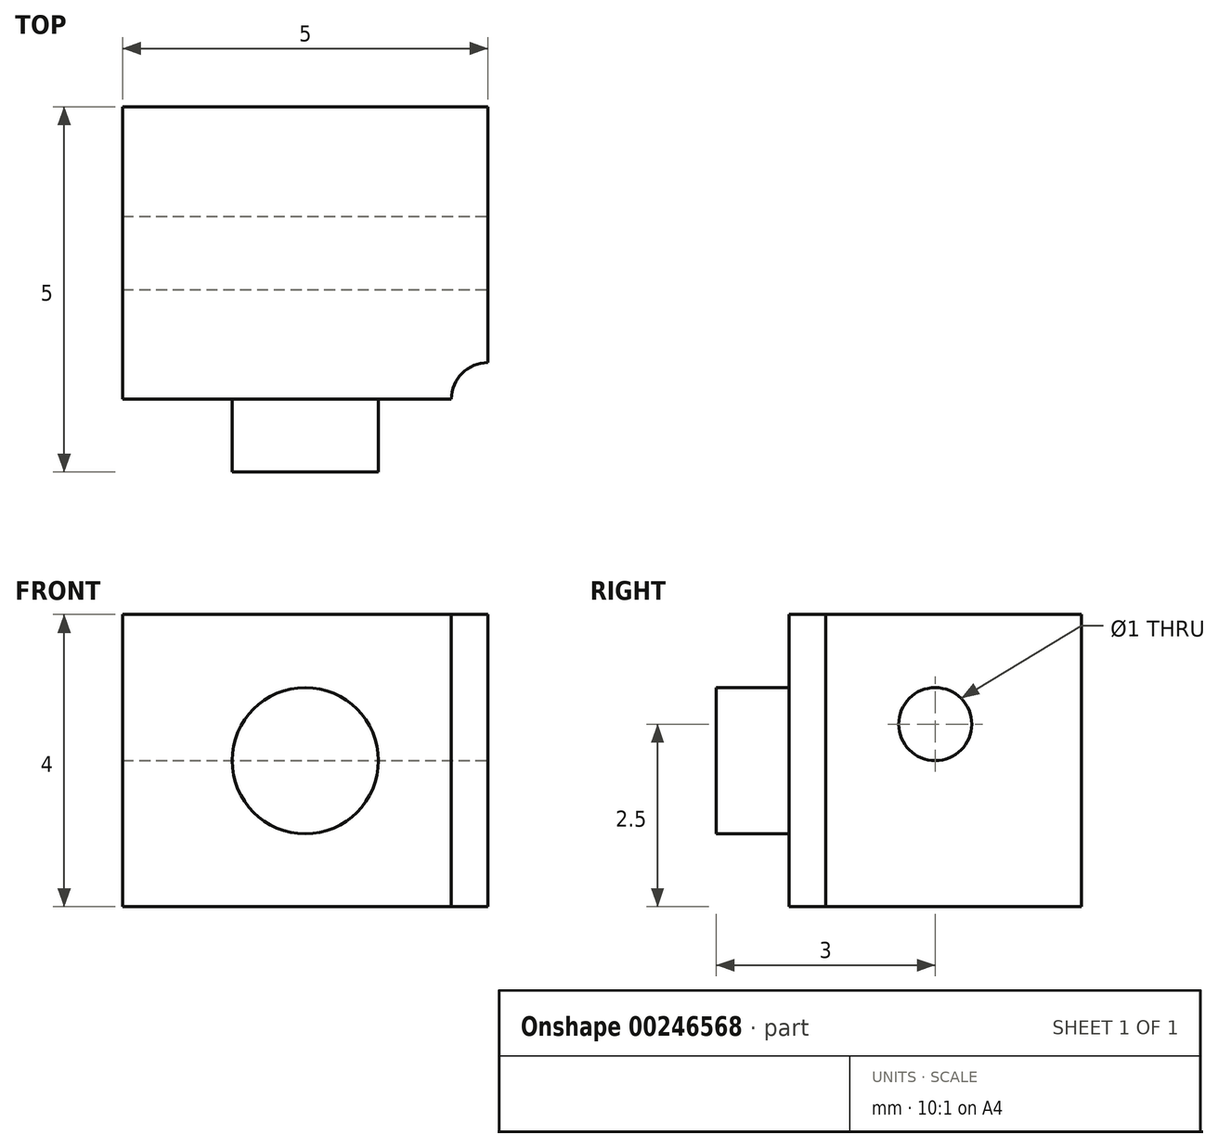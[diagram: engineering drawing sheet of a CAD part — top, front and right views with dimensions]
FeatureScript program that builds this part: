
annotation { "Feature Type Name" : "Feature", "Feature Type Description" : "" }
export const myFeature = defineFeature(function(context is Context, id is Id, definition is map)
    precondition{}
    {
        {
            var Q0;
            Q0=qCreatedBy(makeId("Top.planeOp"),FACE);
            var sketch = newSketch(context, id + "F0", { "sketchPlane" : qUnion([Q0])});
            skLineSegment(sketch, "E0.bottom", {"start": v(0, 0) * mm, "end": v(5, 0) * mm});
            skLineSegment(sketch, "E0.top", {"start": v(0, 4) * mm, "end": v(5, 4) * mm});
            skLineSegment(sketch, "E0.left", {"start": v(0, 0) * mm, "end": v(0, 4) * mm});
            skLineSegment(sketch, "E0.right", {"start": v(5, 0) * mm, "end": v(5, 4) * mm});
            skSolve(sketch);
        }
        {
            var Q0;
            Q0=makeQuery(id+"F0.imprint","IMPRINT",FACE,{"disambiguationData":[TD([[makeQuery(id+"F0.imprint","IMPRINT",EDGE,{"derivedFrom":sQuery(id+"F0.wireOp",EDGE,"E0.bottom")}),1.0]])]});
            extrude(context, id + "F1", {"entities" : qUnion([Q0]), "depth" : 4 * mm});
        }
        {
            var Q0;
            Q0=makeQuery(id+"F1.opExtrude","SWEPT_FACE",FACE,{"disambiguationData":[OSD([sQuery(id+"F0.wireOp",EDGE,"E0.bottom")])]});
            var sketch = newSketch(context, id + "F2", { "sketchPlane" : qUnion([Q0])});
            skCircle(sketch, "E1", {"center": v(2.5, 2) * mm, "radius": 1 * mm});
            skSolve(sketch);
        }
        {
            var Q0;
            Q0=makeQuery(id+"F2.imprint","IMPRINT",FACE,{"disambiguationData":[TD([[makeQuery(id+"F2.imprint","IMPRINT",EDGE,{"derivedFrom":sQuery(id+"F2.wireOp",EDGE,"E1")}),1.0]])]});
            extrude(context, id + "F3", {"entities" : qUnion([Q0]), "operationType" : NewBodyOperationType.ADD, "depth" : 1 * mm});
        }
        {
            var Q0;
            Q0=makeQuery(id+"F1.opExtrude","CAP_FACE",FACE,{"disambiguationData":[OSD([sQuery(id+"F0.wireOp",EDGE,"E0.bottom"),sQuery(id+"F0.wireOp",EDGE,"E0.top"),sQuery(id+"F0.wireOp",EDGE,"E0.left"),sQuery(id+"F0.wireOp",EDGE,"E0.right")])],"isStart":false});
            var sketch = newSketch(context, id + "F4", { "sketchPlane" : qUnion([Q0])});
            skCircle(sketch, "E2", {"center": v(5, 0) * mm, "radius": 0.5 * mm});
            skSolve(sketch);
        }
        {
            var Q0;
            {var subQ0=sQuery(id+"F4.wireOp",EDGE,"E2");var subQ1=makeQuery(id+"F1.opExtrude","CAP_EDGE",EDGE,{"disambiguationData":[OSD([sQuery(id+"F0.wireOp",EDGE,"E0.bottom")])],"isStart":false});var subQ2=makeQuery(id+"F4.imprint","INTERSECT",VERTEX,{"derivedFrom":[subQ1,subQ0]});Q0=makeQuery(id+"F4.imprint","IMPRINT",FACE,{"disambiguationData":[TD([[makeQuery(id+"F4.imprint","IMPRINT",EDGE,{"disambiguationData":[TD([[subQ2,-1.0]])],"derivedFrom":subQ0}),1.0]])]});}
            var Q1;
            {var subQ0=sQuery(id+"F4.wireOp",EDGE,"E2");var subQ1=makeQuery(id+"F1.opExtrude","CAP_EDGE",EDGE,{"disambiguationData":[OSD([sQuery(id+"F0.wireOp",EDGE,"E0.bottom")])],"isStart":false});var subQ2=makeQuery(id+"F4.imprint","INTERSECT",VERTEX,{"derivedFrom":[subQ1,subQ0]});Q1=makeQuery(id+"F4.imprint","IMPRINT",FACE,{"disambiguationData":[TD([[makeQuery(id+"F4.imprint","IMPRINT",EDGE,{"disambiguationData":[TD([[subQ2,1.0]])],"derivedFrom":subQ0}),1.0]])]});}
            var Q2;
            Q2=sQuery(id+"F4.wireOp",EDGE,"E2");
            extrude(context, id + "F5", {"entities" : qUnion([Q0, Q1]), "operationType" : NewBodyOperationType.REMOVE, "surfaceEntities" : qUnion([Q2]), "oppositeDirection" : true, "depth" : 25 * mm});
        }
        {
            var Q0;
            Q0=makeQuery(id+"F1.opExtrude","SWEPT_FACE",FACE,{"disambiguationData":[OSD([sQuery(id+"F0.wireOp",EDGE,"E0.right")])]});
            var sketch = newSketch(context, id + "F6", { "sketchPlane" : qUnion([Q0])});
            skCircle(sketch, "E3", {"center": v(2, 2.5) * mm, "radius": 0.5 * mm});
            skSolve(sketch);
        }
        {
            var Q0;
            Q0=makeQuery(id+"F6.imprint","IMPRINT",FACE,{"disambiguationData":[TD([[makeQuery(id+"F6.imprint","IMPRINT",EDGE,{"derivedFrom":sQuery(id+"F6.wireOp",EDGE,"E3")}),1.0]])]});
            var Q1;
            Q1=sQuery(id+"F6.wireOp",EDGE,"E3");
            extrude(context, id + "F7", {"entities" : qUnion([Q0]), "operationType" : NewBodyOperationType.REMOVE, "surfaceEntities" : qUnion([Q1]), "oppositeDirection" : true, "depth" : 5 * mm});
        }
    });
